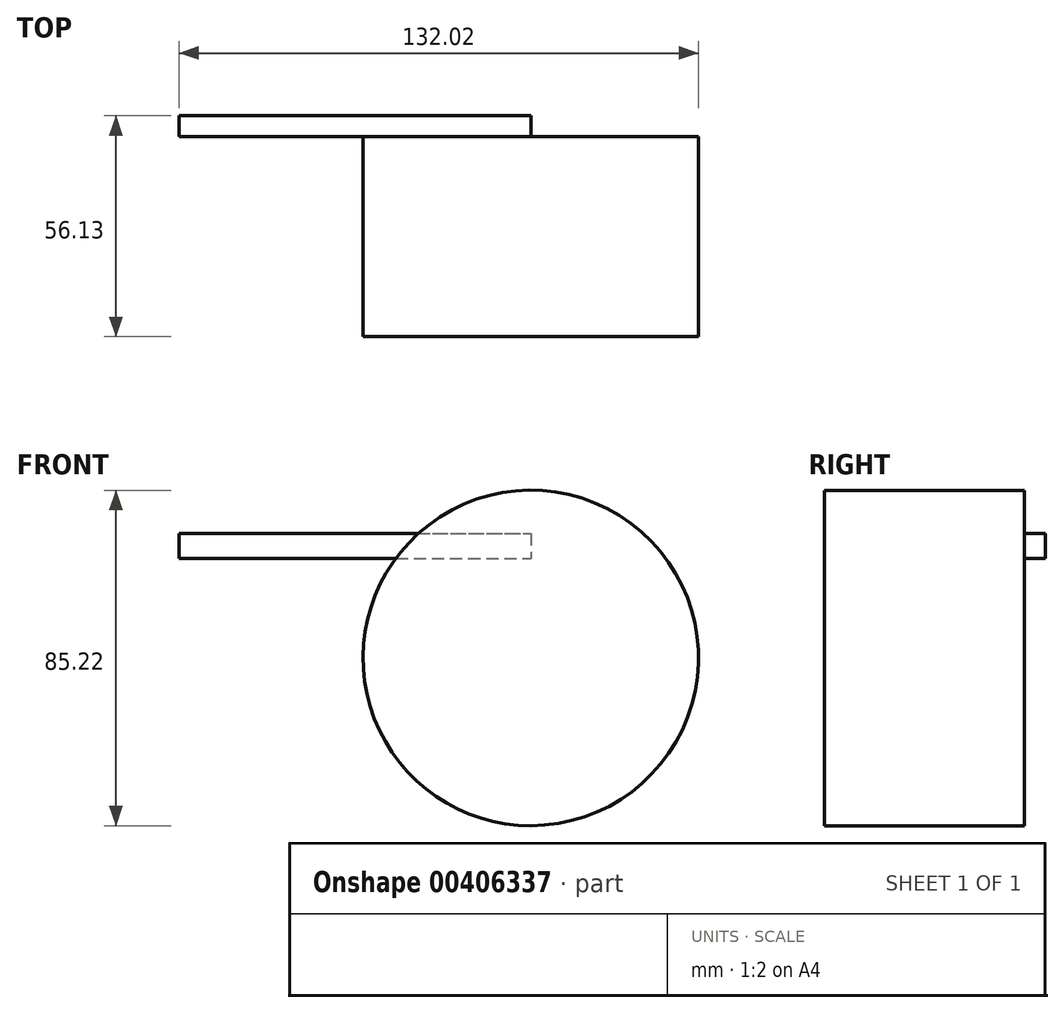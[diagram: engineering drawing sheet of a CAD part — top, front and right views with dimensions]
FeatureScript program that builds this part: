
annotation { "Feature Type Name" : "Feature", "Feature Type Description" : "" }
export const myFeature = defineFeature(function(context is Context, id is Id, definition is map)
    precondition{}
    {
        {
            var Q0;
            Q0=qCreatedBy(makeId("Front.planeOp"),FACE);
            var sketch = newSketch(context, id + "F0", { "sketchPlane" : qUnion([Q0])});
            skCircle(sketch, "E0", {"center": v(0, 0) * mm, "radius": 42.61 * mm});
            skCircle(sketch, "E1", {"center": v(0, 0) * mm, "radius": 6.75 * mm});
            skSolve(sketch);
        }
        {
            var Q0;
            Q0=makeQuery(id+"F0.imprint","IMPRINT",FACE,{"disambiguationData":[TD([[makeQuery(id+"F0.imprint","IMPRINT",EDGE,{"derivedFrom":sQuery(id+"F0.wireOp",EDGE,"E1")}),1.0]])]});
            var Q1;
            Q1=makeQuery(id+"F0.imprint","IMPRINT",FACE,{"disambiguationData":[TD([[makeQuery(id+"F0.imprint","IMPRINT",EDGE,{"derivedFrom":sQuery(id+"F0.wireOp",EDGE,"E0")}),1.0]])]});
            extrude(context, id + "F1", {"entities" : qUnion([Q0, Q1]), "depth" : 25.4 * mm});
        }
        {
            var Q0;
            Q0=makeQuery(id+"F1.opExtrude","CAP_FACE",FACE,{"disambiguationData":[OSD([sQuery(id+"F0.wireOp",EDGE,"E0")])],"isStart":false});
            extrude(context, id + "F2", {"entities" : qUnion([Q0]), "operationType" : NewBodyOperationType.ADD, "depth" : 25.4 * mm});
        }
        {
            var Q0;
            Q0=qCreatedBy(makeId("Front.planeOp"),FACE);
            var sketch = newSketch(context, id + "F3", { "sketchPlane" : qUnion([Q0])});
            skLineSegment(sketch, "E2.bottom", {"start": v(-89.4, 31.57) * mm, "end": v(0, 31.57) * mm});
            skLineSegment(sketch, "E2.top", {"start": v(-89.4, 25.3) * mm, "end": v(0, 25.3) * mm});
            skLineSegment(sketch, "E2.left", {"start": v(-89.4, 31.57) * mm, "end": v(-89.4, 25.3) * mm});
            skLineSegment(sketch, "E2.right", {"start": v(0, 31.57) * mm, "end": v(0, 25.3) * mm});
            skSolve(sketch);
        }
        {
            var Q0;
            Q0 = qSketchRegion(id + "F3", true);
            extrude(context, id + "F4", {"entities" : qUnion([Q0]), "operationType" : NewBodyOperationType.ADD, "oppositeDirection" : true, "depth" : 5.33 * mm});
        }
    });
